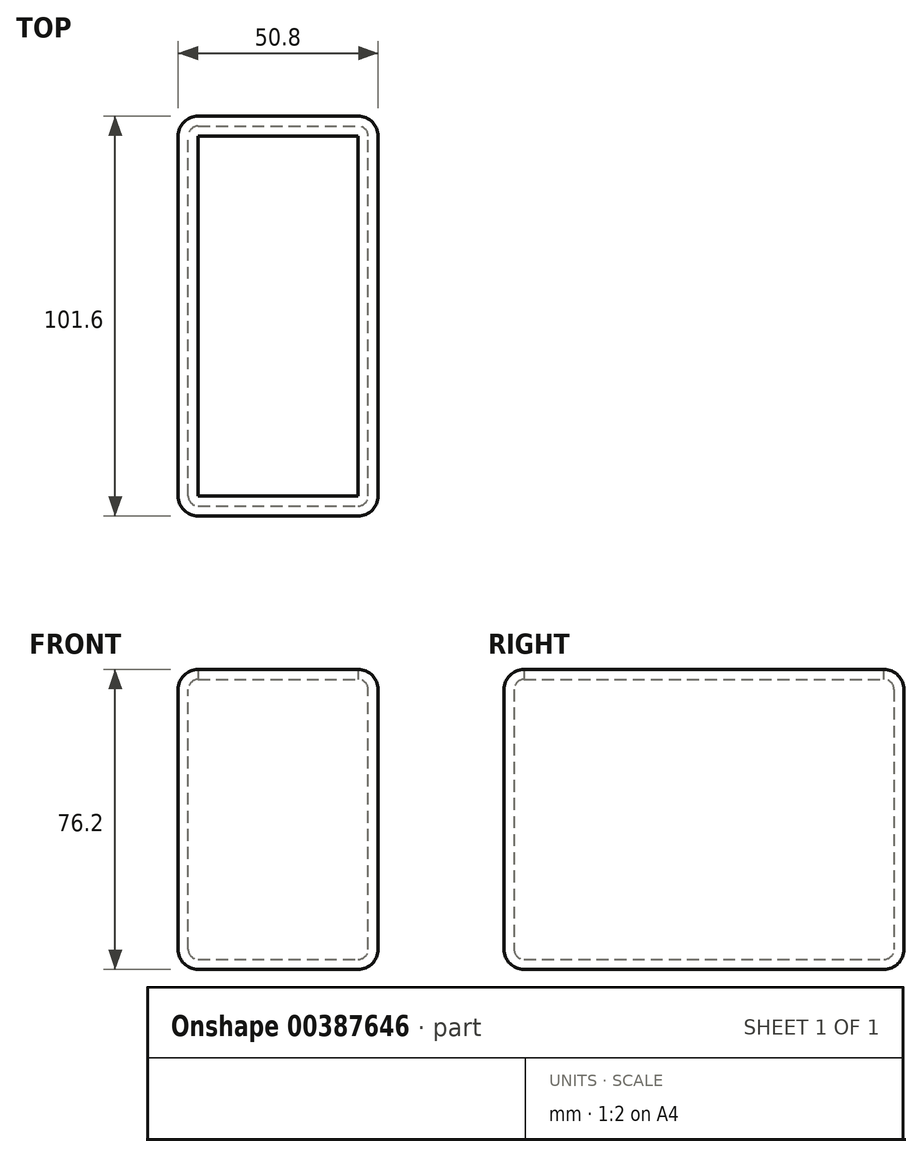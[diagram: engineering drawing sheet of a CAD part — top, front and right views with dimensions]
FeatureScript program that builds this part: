
annotation { "Feature Type Name" : "Feature", "Feature Type Description" : "" }
export const myFeature = defineFeature(function(context is Context, id is Id, definition is map)
    precondition{}
    {
        {
            var Q0;
            Q0=qCreatedBy(makeId("Top.planeOp"),FACE);
            var sketch = newSketch(context, id + "F0", { "sketchPlane" : qUnion([Q0])});
            skLineSegment(sketch, "E0.bottom", {"start": v(25.4, -50.8) * mm, "end": v(-25.4, -50.8) * mm});
            skLineSegment(sketch, "E0.top", {"start": v(25.4, 50.8) * mm, "end": v(-25.4, 50.8) * mm});
            skLineSegment(sketch, "E0.left", {"start": v(25.4, -50.8) * mm, "end": v(25.4, 50.8) * mm});
            skLineSegment(sketch, "E0.right", {"start": v(-25.4, -50.8) * mm, "end": v(-25.4, 50.8) * mm});
            skPoint(sketch, "E0.middle", {"position": v(0, 0) * mm});
            skSolve(sketch);
        }
        {
            var Q0;
            Q0 = qSketchRegion(id + "F0", true);
            extrude(context, id + "F1", {"entities" : qUnion([Q0]), "depth" : 76.2 * mm});
        }
        {
            var Q0;
            Q0=makeQuery(id+"F1.opExtrude","CAP_EDGE",EDGE,{"disambiguationData":[OSD([sQuery(id+"F0.wireOp",EDGE,"E0.right")])],"isStart":false});
            var Q1;
            Q1=makeQuery(id+"F1.opExtrude","CAP_EDGE",EDGE,{"disambiguationData":[OSD([sQuery(id+"F0.wireOp",EDGE,"E0.top")])],"isStart":false});
            var Q2;
            Q2=makeQuery(id+"F1.opExtrude","SWEPT_EDGE",EDGE,{"disambiguationData":[OSD([sQuery(id+"F0.wireOp",EDGE,"E0.top"),sQuery(id+"F0.wireOp",EDGE,"E0.right")])]});
            var Q3;
            Q3=makeQuery(id+"F1.opExtrude","SWEPT_EDGE",EDGE,{"disambiguationData":[OSD([sQuery(id+"F0.wireOp",EDGE,"E0.bottom"),sQuery(id+"F0.wireOp",EDGE,"E0.right")])]});
            var Q4;
            Q4=makeQuery(id+"F1.opExtrude","CAP_EDGE",EDGE,{"disambiguationData":[OSD([sQuery(id+"F0.wireOp",EDGE,"E0.bottom")])],"isStart":false});
            var Q5;
            Q5=makeQuery(id+"F1.opExtrude","CAP_EDGE",EDGE,{"disambiguationData":[OSD([sQuery(id+"F0.wireOp",EDGE,"E0.left")])],"isStart":false});
            var Q6;
            Q6=makeQuery(id+"F1.opExtrude","SWEPT_EDGE",EDGE,{"disambiguationData":[OSD([sQuery(id+"F0.wireOp",EDGE,"E0.bottom"),sQuery(id+"F0.wireOp",EDGE,"E0.left")])]});
            var Q7;
            Q7=makeQuery(id+"F1.opExtrude","SWEPT_EDGE",EDGE,{"disambiguationData":[OSD([sQuery(id+"F0.wireOp",EDGE,"E0.top"),sQuery(id+"F0.wireOp",EDGE,"E0.left")])]});
            var Q8;
            Q8=makeQuery(id+"F1.opExtrude","CAP_EDGE",EDGE,{"disambiguationData":[OSD([sQuery(id+"F0.wireOp",EDGE,"E0.top")])],"isStart":true});
            var Q9;
            Q9=makeQuery(id+"F1.opExtrude","CAP_EDGE",EDGE,{"disambiguationData":[OSD([sQuery(id+"F0.wireOp",EDGE,"E0.left")])],"isStart":true});
            var Q10;
            Q10=makeQuery(id+"F1.opExtrude","CAP_EDGE",EDGE,{"disambiguationData":[OSD([sQuery(id+"F0.wireOp",EDGE,"E0.right")])],"isStart":true});
            var Q11;
            Q11=makeQuery(id+"F1.opExtrude","CAP_EDGE",EDGE,{"disambiguationData":[OSD([sQuery(id+"F0.wireOp",EDGE,"E0.bottom")])],"isStart":true});
            fillet(context, id + "F2", {"entities" : qUnion([Q0, Q1, Q2, Q3, Q4, Q5, Q6, Q7, Q8, Q9, Q10, Q11]), "radius" : 5.08 * mm, "tangentPropagation" : true, "allowEdgeOverflow" : false});
        }
        {
            var Q0;
            Q0=makeQuery(id+"F1.opExtrude","CAP_FACE",FACE,{"disambiguationData":[OSD([sQuery(id+"F0.wireOp",EDGE,"E0.bottom"),sQuery(id+"F0.wireOp",EDGE,"E0.top"),sQuery(id+"F0.wireOp",EDGE,"E0.left"),sQuery(id+"F0.wireOp",EDGE,"E0.right")])],"isStart":false});
            shell(context, id + "F3", {"entities" : qUnion([Q0]), "thickness" : 2.54 * mm});
        }
    });
